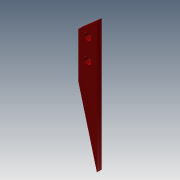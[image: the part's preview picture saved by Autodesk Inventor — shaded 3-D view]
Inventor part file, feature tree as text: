
AUTODESK INVENTOR PART (.ipt)
format: ipt  version: 2013 (Build 170138000, 138)  size: 82,432 bytes
history: native  units: mm
features: extrude x1, sketch x1
ambient origin geometry x8: Origin, YZ Plane, XZ Plane, XY Plane, X Axis, Y Axis, Z Axis, Center Point
bodies: Solid1 (feature_tree)
feature tree (2):
  extrude  "Extrusion1"  Depth=10.0mm
  sketch  "Sketch1"  dims[d2=27.0mm d9=10.0mm d10=3.0mm d13=20.0mm d14=9.0mm d15=3.0mm d16=2.0mm d17=0.0mm]
